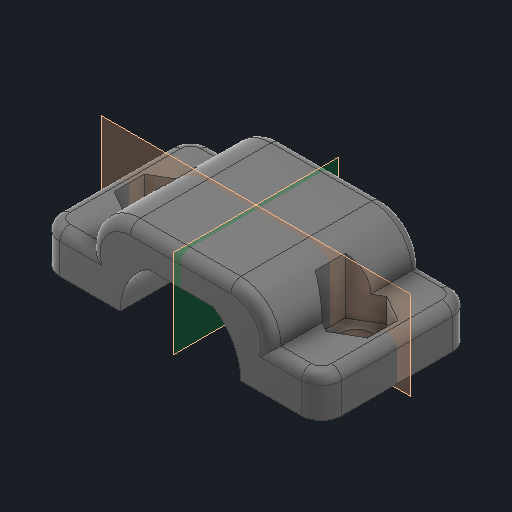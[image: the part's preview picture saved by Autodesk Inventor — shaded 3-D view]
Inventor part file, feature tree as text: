
AUTODESK INVENTOR PART (.ipt)
format: ipt  version: 2024 (Build 280153000, 153)  size: 267,264 bytes
history: native  units: in
note: dims shown in document units (in); Inventor stores cm internally (conversion verified against a paired STEP export)
features: sketch x3, extrude x2, plane x2, fillet x2, hole x1, mirror x1
ambient origin geometry x8: Origin, YZ Plane, XZ Plane, XY Plane, X Axis, Y Axis, Z Axis, Center Point
bodies: Solid1 (feature_tree)
feature tree (11):
  extrude  "Extrusion2"  Depth=0.1181in TaperAngle=0.0deg
  plane  "Work Plane1"
  extrude  "Extrusion3"  Depth=0.1575in
  hole  "Hole1"  [1 undecoded]
  mirror  "Mirror1"
  plane  "Work Plane2"
  fillet  "Fillet3"  Radius=0.2953in
  fillet  "Fillet4"  Radius=0.0787in
  sketch  "Sketch3"  dims[d20=0.1575in d21=0.1969in d22=0.315in d23=0.1181in d24=0.5906in d25=0.0in]
  sketch  "Sketch4"  dims[d26=0.2366in d27=0.1575in]
  sketch  "Sketch5"  dims[d28=0.315in d29=0.0945in d30=0.0in d31=0.0in d32=0.122in d33=0.2362in d34=0.1575in d35=0.0787in d36=90.0deg d37=0.315in d38=0.8108in d39=0.2953in d40=0.2953in d42=0.0787in d43=0.0394in]
note: 1 required parameter value undecoded (feature->parameter linkage not recoverable at this tier; creation-order binding heuristic only, values carry confidence <= 0.55)
